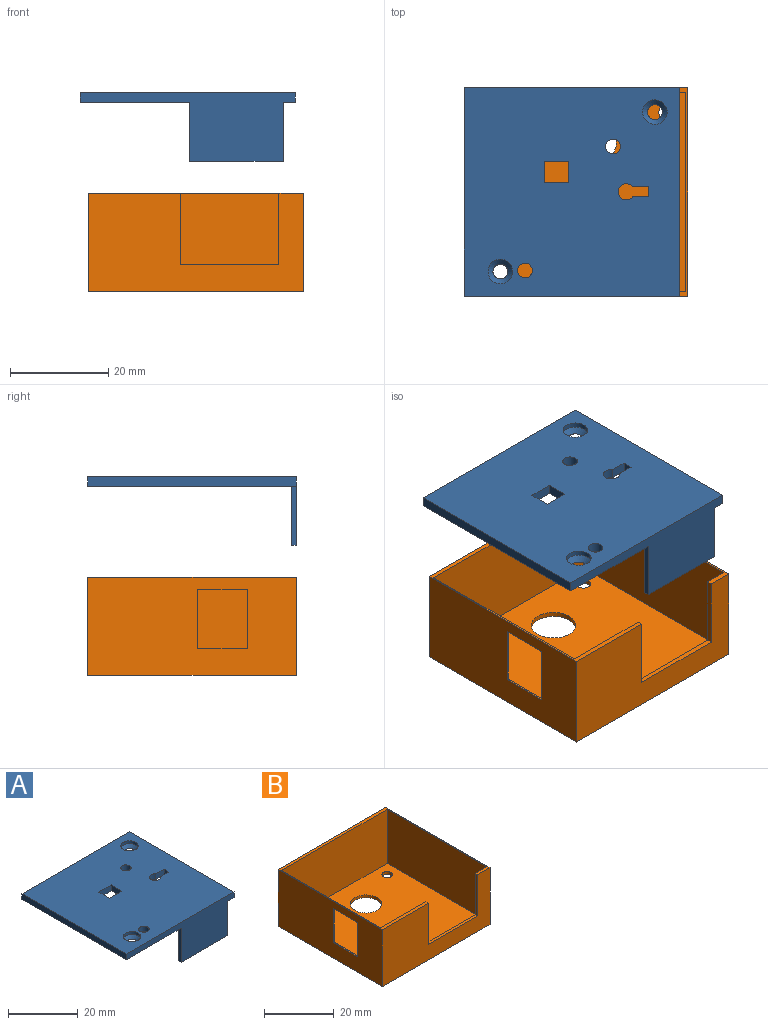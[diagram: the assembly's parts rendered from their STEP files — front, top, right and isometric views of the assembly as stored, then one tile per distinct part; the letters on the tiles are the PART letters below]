
ASSEMBLY  parts=2 mates=1
PART A: 24 faces, bbox 43.7x42.4x14 mm
  f0: plane 43.7x14mm, normal (0,-1,0), area 315.4mm2, adj f1,f13,f14,f19,f20,f22,f23
  f1: plane 42.4x2mm, normal (1,0,0), area 84.8mm2, adj f0,f2,f14,f19
  f2: plane 43.7x2mm, normal (0,1,0), area 87.4mm2, adj f1,f13,f14,f19
  f3: plane 5x2mm, normal (0,-1,0), area 10mm2, adj f4,f9,f14,f19
  f4: plane 4.4x2mm, normal (-1,0,0), area 8.8mm2, adj f3,f5,f14,f19
  f5: plane 5x2mm, normal (0,1,0), area 10mm2, adj f4,f9,f14,f19
  f6: cylinder r=1.65mm len=3.3mm, axis (0,0,-1), area 16.4mm2, adj f7,f10,f14,f19
  f7: plane 3.3x2mm, normal (0,-1,0), area 6.6mm2, adj f6,f8,f14,f19
  f8: plane 2x2mm, normal (-1,0,0), area 4mm2, adj f7,f10,f14,f19
  f9: plane 4.4x2mm, normal (1,0,0), area 8.8mm2, adj f3,f5,f14,f19
  f10: plane 3.3x2mm, normal (0,1,0), area 6.6mm2, adj f6,f8,f14,f19
  f11: cylinder r=1.5mm len=3mm, axis (0,0,-1), area 18.8mm2, adj f14,f19
  f12: cylinder r=1.5mm len=3mm, axis (0,0,-1), area 18.8mm2, adj f14,f19
  f13: plane 42.4x2mm, normal (-1,0,0), area 84.8mm2, adj f0,f2,f14,f19
  f14: plane 43.7x42.4mm, normal (0,0,-1), area 1768.9mm2, adj f0,f1,f2,f3,f4,f5,f6,f7
  f15: cone r=1.5mm half-angle=45deg, axis (0,0,1), area 17.8mm2, adj f14,f18
  f16: cone r=1.5mm half-angle=45deg, axis (0,0,1), area 17.8mm2, adj f14,f17
  f17: cylinder r=2.5mm len=5mm, axis (0,0,-1), area 15.7mm2, adj f16,f19
  f18: cylinder r=2.5mm len=5mm, axis (0,0,-1), area 15.7mm2, adj f15,f19
  f19: plane 43.7x42.4mm, normal (0,0,1), area 1762.8mm2, adj f0,f1,f2,f3,f4,f5,f6,f7
  f20: plane 12x1mm, normal (1,0,0), area 12mm2, adj f0,f14,f21,f23
  f21: plane 19x12mm, normal (0,1,0), area 228mm2, adj f14,f20,f22,f23
  f22: plane 12x1mm, normal (-1,0,0), area 12mm2, adj f0,f14,f21,f23
  f23: plane 19x1mm, normal (0,0,-1), area 19mm2, adj f0,f20,f21,f22
PART B: 25 faces, bbox 43.7x42.4x20 mm
  f0: plane 43.7x42.4mm, normal (0,0,-1), area 1768.1mm2, adj f3,f4,f5,f6,f11,f12,f13,f21
  f1: plane 43x40.4mm, normal (0,0,1), area 1652.4mm2, adj f7,f8,f9,f10,f11,f12,f13,f21
  f2: plane 43.7x42.4mm, normal (0,0,1), area 95.7mm2, adj f3,f4,f5,f6,f7,f8,f9,f10
  f3: plane 42.4x20mm, normal (-1,0,0), area 728mm2, adj f0,f2,f4,f6,f14,f15,f16,f17
  f4: plane 43.7x20mm, normal (0,-1,0), area 584mm2, adj f0,f2,f3,f5,f18,f19,f20
  f5: plane 42.4x20mm, normal (1,0,0), area 848mm2, adj f0,f2,f4,f6
  f6: plane 43.7x20mm, normal (0,1,0), area 874mm2, adj f0,f2,f3,f5
  f7: plane 40.4x19mm, normal (-1,0,0), area 767.6mm2, adj f1,f2,f8,f10
  f8: plane 43x19mm, normal (0,-1,0), area 817mm2, adj f1,f2,f7,f9
  f9: plane 40.4x19mm, normal (1,0,0), area 647.6mm2, adj f1,f2,f8,f10,f14,f15,f16,f17
  f10: plane 43x19mm, normal (0,1,0), area 527mm2, adj f1,f2,f7,f9,f18,f19,f20
  f11: cylinder r=1.5mm len=3mm, axis (0,0,1), area 9.4mm2, adj f0,f1
  f12: cylinder r=1.5mm len=3mm, axis (0,0,1), area 9.4mm2, adj f0,f1
  f13: cylinder r=4.5mm len=9mm, axis (0,0,1), area 28.3mm2, adj f0,f1
  f14: plane 12x0.35mm, normal (0,1,0), area 4.2mm2, adj f3,f9,f15,f17
  f15: plane 10x0.35mm, normal (0,0,-1), area 3.5mm2, adj f3,f9,f14,f16
  f16: plane 12x0.35mm, normal (0,-1,0), area 4.2mm2, adj f3,f9,f15,f17
  f17: plane 10x0.35mm, normal (0,0,1), area 3.5mm2, adj f3,f9,f14,f16
  f18: plane 14.5x1mm, normal (-1,0,0), area 14.5mm2, adj f2,f4,f10,f20
  f19: plane 14.5x1mm, normal (1,0,0), area 14.5mm2, adj f2,f4,f10,f20
  f20: plane 20x1mm, normal (0,0,1), area 20mm2, adj f4,f10,f18,f19
  f21: plane 3.5x1mm, normal (0,1,0), area 3.5mm2, adj f0,f1,f22,f24
  f22: plane 2x1mm, normal (1,0,0), area 2mm2, adj f0,f1,f21,f23
  f23: plane 3.5x1mm, normal (0,-1,0), area 3.5mm2, adj f0,f1,f22,f24
  f24: plane 2x1mm, normal (-1,0,0), area 2mm2, adj f0,f1,f21,f23
PLACE A rot(axis=(-0.03,-1,0.01),0deg) t=(44.76,-30.78,45.9)mm
PLACE B rot(axis=(-0.03,-1,0.01),0deg) t=(29.5,-27.67,7.49)mm
MATE slider A.f15 <-> B.f12  axis (0,0,-1) through (-8.55,-17.86,45.9)mm
